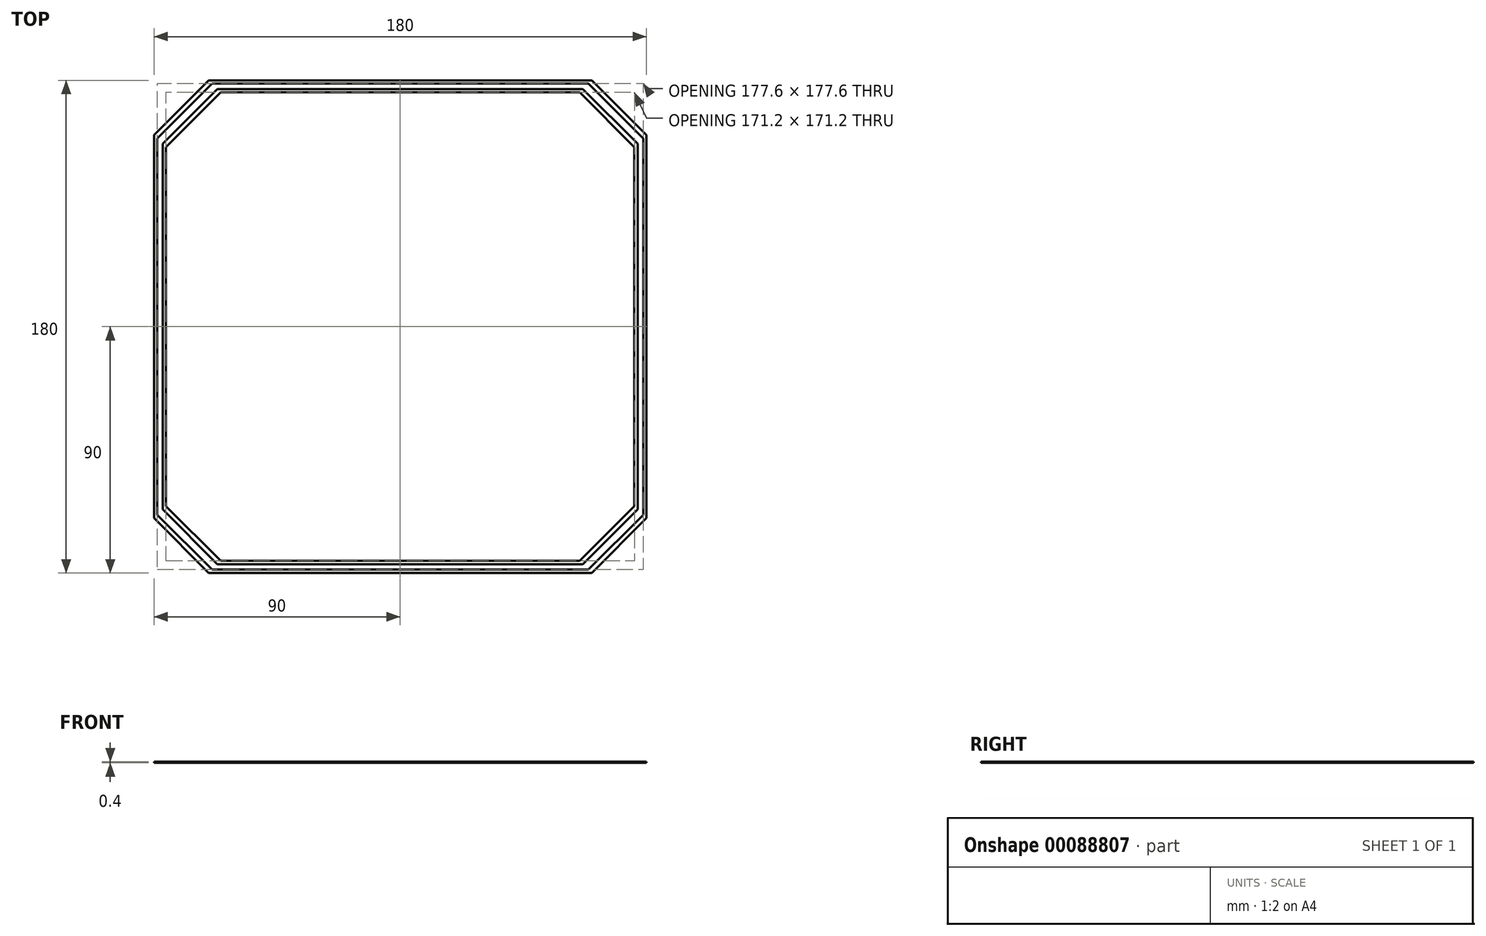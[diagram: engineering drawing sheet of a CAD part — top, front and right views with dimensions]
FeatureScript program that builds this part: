
annotation { "Feature Type Name" : "Feature", "Feature Type Description" : "" }
export const myFeature = defineFeature(function(context is Context, id is Id, definition is map)
    precondition{}
    {
        {
            var Q0;
            Q0=qCreatedBy(makeId("Top.planeOp"),FACE);
            var sketch = newSketch(context, id + "F0", { "sketchPlane" : qUnion([Q0])});
            skLineSegment(sketch, "E0.bottom", {"start": v(68.8, 88.8) * mm, "end": v(-68.8, 88.8) * mm});
            skLineSegment(sketch, "E0.top", {"start": v(68.8, -88.8) * mm, "end": v(-68.8, -88.8) * mm});
            skLineSegment(sketch, "E0.left", {"start": v(88.8, 68.8) * mm, "end": v(88.8, -68.8) * mm});
            skLineSegment(sketch, "E0.right", {"start": v(-88.8, 68.8) * mm, "end": v(-88.8, -68.8) * mm});
            skPoint(sketch, "E0.middle", {"position": v(0, 0) * mm});
            skLineSegment(sketch, "E1.bottom", {"start": v(70, 90) * mm, "end": v(-70, 90) * mm});
            skLineSegment(sketch, "E1.top", {"start": v(70, -90) * mm, "end": v(-70, -90) * mm});
            skLineSegment(sketch, "E1.left", {"start": v(90, 70) * mm, "end": v(90, -70) * mm});
            skLineSegment(sketch, "E1.right", {"start": v(-90, 70) * mm, "end": v(-90, -70) * mm});
            skLineSegment(sketch, "E2.bottom", {"start": v(-66.8, -86.8) * mm, "end": v(66.8, -86.8) * mm});
            skLineSegment(sketch, "E2.top", {"start": v(-66.8, 86.8) * mm, "end": v(66.8, 86.8) * mm});
            skLineSegment(sketch, "E2.left", {"start": v(-86.8, -66.8) * mm, "end": v(-86.8, 66.8) * mm});
            skLineSegment(sketch, "E2.right", {"start": v(86.8, -66.8) * mm, "end": v(86.8, 66.8) * mm});
            skLineSegment(sketch, "E3.bottom", {"start": v(-65.6, -85.6) * mm, "end": v(65.6, -85.6) * mm});
            skLineSegment(sketch, "E3.top", {"start": v(-65.6, 85.6) * mm, "end": v(65.6, 85.6) * mm});
            skLineSegment(sketch, "E3.left", {"start": v(-85.6, -65.6) * mm, "end": v(-85.6, 65.6) * mm});
            skLineSegment(sketch, "E3.right", {"start": v(85.6, -65.6) * mm, "end": v(85.6, 65.6) * mm});
            skPoint(sketch, "E4.visualSharp", {"position": v(-85.6, -85.6) * mm});
            skPoint(sketch, "E5.visualSharp", {"position": v(-86.8, -86.8) * mm});
            skPoint(sketch, "E6.visualSharp", {"position": v(-88.8, -88.8) * mm});
            skPoint(sketch, "E7.visualSharp", {"position": v(-90, -90) * mm});
            skLineSegment(sketch, "E8", {"start": v(-90, -70) * mm, "end": v(-70, -90) * mm});
            skLineSegment(sketch, "E9", {"start": v(-68.8, -88.8) * mm, "end": v(-88.8, -68.8) * mm});
            skLineSegment(sketch, "E10", {"start": v(-86.8, -66.8) * mm, "end": v(-66.8, -86.8) * mm});
            skLineSegment(sketch, "E11", {"start": v(-65.6, -85.6) * mm, "end": v(-85.6, -65.6) * mm});
            skLineSegment(sketch, "E12", {"start": v(-85.6, 65.6) * mm, "end": v(-65.6, 85.6) * mm});
            skLineSegment(sketch, "E13", {"start": v(-66.8, 86.8) * mm, "end": v(-86.8, 66.8) * mm});
            skLineSegment(sketch, "E14", {"start": v(-88.8, 68.8) * mm, "end": v(-68.8, 88.8) * mm});
            skLineSegment(sketch, "E15", {"start": v(-70, 90) * mm, "end": v(-90, 70) * mm});
            skLineSegment(sketch, "E16", {"start": v(0, 0) * mm, "end": v(0, 48.82) * mm});
            skPoint(sketch, "E17.MirrorP", {"position": v(85.6, -85.6) * mm});
            skLineSegment(sketch, "E18.MirrorCS", {"start": v(66.8, 86.8) * mm, "end": v(86.8, 66.8) * mm});
            skLineSegment(sketch, "E19.MirrorCS", {"start": v(68.8, -88.8) * mm, "end": v(88.8, -68.8) * mm});
            skPoint(sketch, "E20.MirrorP", {"position": v(90, -90) * mm});
            skLineSegment(sketch, "E21.MirrorCS", {"start": v(65.6, -85.6) * mm, "end": v(85.6, -65.6) * mm});
            skLineSegment(sketch, "E22.MirrorCS", {"start": v(85.6, 65.6) * mm, "end": v(65.6, 85.6) * mm});
            skPoint(sketch, "E23.MirrorP", {"position": v(86.8, -86.8) * mm});
            skLineSegment(sketch, "E24.MirrorCS", {"start": v(70, 90) * mm, "end": v(90, 70) * mm});
            skLineSegment(sketch, "E25.MirrorCS", {"start": v(88.8, 68.8) * mm, "end": v(68.8, 88.8) * mm});
            skPoint(sketch, "E26.MirrorP", {"position": v(88.8, -88.8) * mm});
            skLineSegment(sketch, "E27.MirrorCS", {"start": v(90, -70) * mm, "end": v(70, -90) * mm});
            skLineSegment(sketch, "E28.MirrorCS", {"start": v(86.8, -66.8) * mm, "end": v(66.8, -86.8) * mm});
            skSolve(sketch);
        }
        {
            var Q0;
            Q0=makeQuery(id+"F0.imprint","IMPRINT",FACE,{"disambiguationData":[TD([[makeQuery(id+"F0.imprint","IMPRINT",EDGE,{"derivedFrom":sQuery(id+"F0.wireOp",EDGE,"E0.bottom")}),-1.0]])]});
            var Q1;
            Q1=makeQuery(id+"F0.imprint","IMPRINT",FACE,{"disambiguationData":[TD([[makeQuery(id+"F0.imprint","IMPRINT",EDGE,{"derivedFrom":sQuery(id+"F0.wireOp",EDGE,"E2.bottom")}),1.0]])]});
            extrude(context, id + "F1", {"entities" : qUnion([Q0, Q1]), "depth" : 0.4 * mm});
        }
    });
